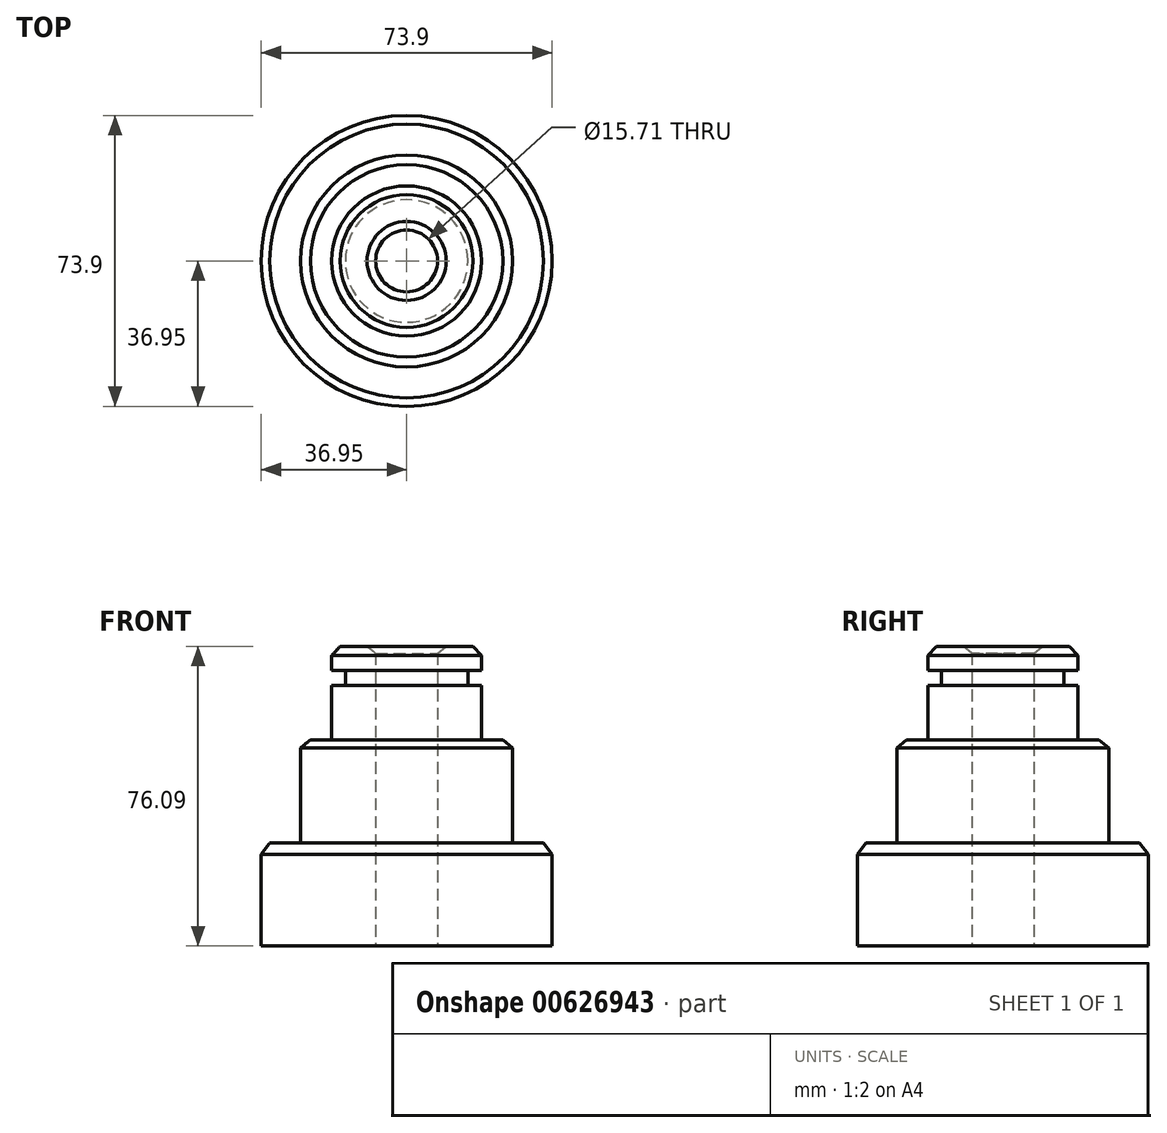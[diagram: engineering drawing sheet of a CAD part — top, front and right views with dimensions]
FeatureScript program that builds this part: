
annotation { "Feature Type Name" : "Feature", "Feature Type Description" : "" }
export const myFeature = defineFeature(function(context is Context, id is Id, definition is map)
    precondition{}
    {
        {
            var Q0;
            Q0=qCreatedBy(makeId("Front.planeOp"),FACE);
            var sketch = newSketch(context, id + "F0", { "sketchPlane" : qUnion([Q0])});
            skLineSegment(sketch, "E0", {"start": v(-7.86, 0) * mm, "end": v(-36.95, 0) * mm});
            skLineSegment(sketch, "E1", {"start": v(-36.95, 0) * mm, "end": v(-36.95, 23.28) * mm});
            skLineSegment(sketch, "E2", {"start": v(-36.95, 23.28) * mm, "end": v(-34.77, 26.19) * mm});
            skLineSegment(sketch, "E3", {"start": v(-34.77, 26.19) * mm, "end": v(-26.91, 26.19) * mm});
            skLineSegment(sketch, "E4", {"start": v(-26.91, 26.19) * mm, "end": v(-26.91, 50.34) * mm});
            skLineSegment(sketch, "E5", {"start": v(-26.91, 50.34) * mm, "end": v(-24.44, 52.37) * mm});
            skLineSegment(sketch, "E6", {"start": v(-24.44, 52.37) * mm, "end": v(-19.06, 52.37) * mm});
            skLineSegment(sketch, "E7", {"start": v(-19.06, 52.37) * mm, "end": v(-19.06, 66.2) * mm});
            skLineSegment(sketch, "E8", {"start": v(-19.06, 66.2) * mm, "end": v(-15.57, 66.2) * mm});
            skLineSegment(sketch, "E9", {"start": v(-15.57, 66.2) * mm, "end": v(-15.57, 69.98) * mm});
            skLineSegment(sketch, "E10", {"start": v(-15.57, 69.98) * mm, "end": v(-19.06, 69.98) * mm});
            skLineSegment(sketch, "E11", {"start": v(-19.06, 69.98) * mm, "end": v(-19.06, 73.76) * mm});
            skLineSegment(sketch, "E12", {"start": v(-19.06, 73.76) * mm, "end": v(-16.88, 76.09) * mm});
            skLineSegment(sketch, "E13", {"start": v(-16.88, 76.09) * mm, "end": v(-10.04, 76.09) * mm});
            skLineSegment(sketch, "E14", {"start": v(-10.04, 76.09) * mm, "end": v(-7.86, 74.34) * mm});
            skLineSegment(sketch, "E15", {"start": v(-7.86, 74.34) * mm, "end": v(-7.86, 0) * mm});
            skLineSegment(sketch, "E16", {"start": v(0, 0) * mm, "end": v(0, 77.1) * mm, "construction": true});
            skSolve(sketch);
        }
        {
            var Q0;
            Q0=makeQuery(id+"F0.imprint","IMPRINT",FACE,{"disambiguationData":[TD([[makeQuery(id+"F0.imprint","IMPRINT",EDGE,{"derivedFrom":sQuery(id+"F0.wireOp",EDGE,"E0")}),-1.0]])]});
            var Q1;
            Q1=sQuery(id+"F0.wireOp",EDGE,"E16");
            revolve(context, id + "F1", {"surfaceOperationType" : NewSurfaceOperationType.NEW, "entities" : qUnion([Q0]), "axis" : qUnion([Q1]), "revolveType" : RevolveType.FULL});
        }
    });
